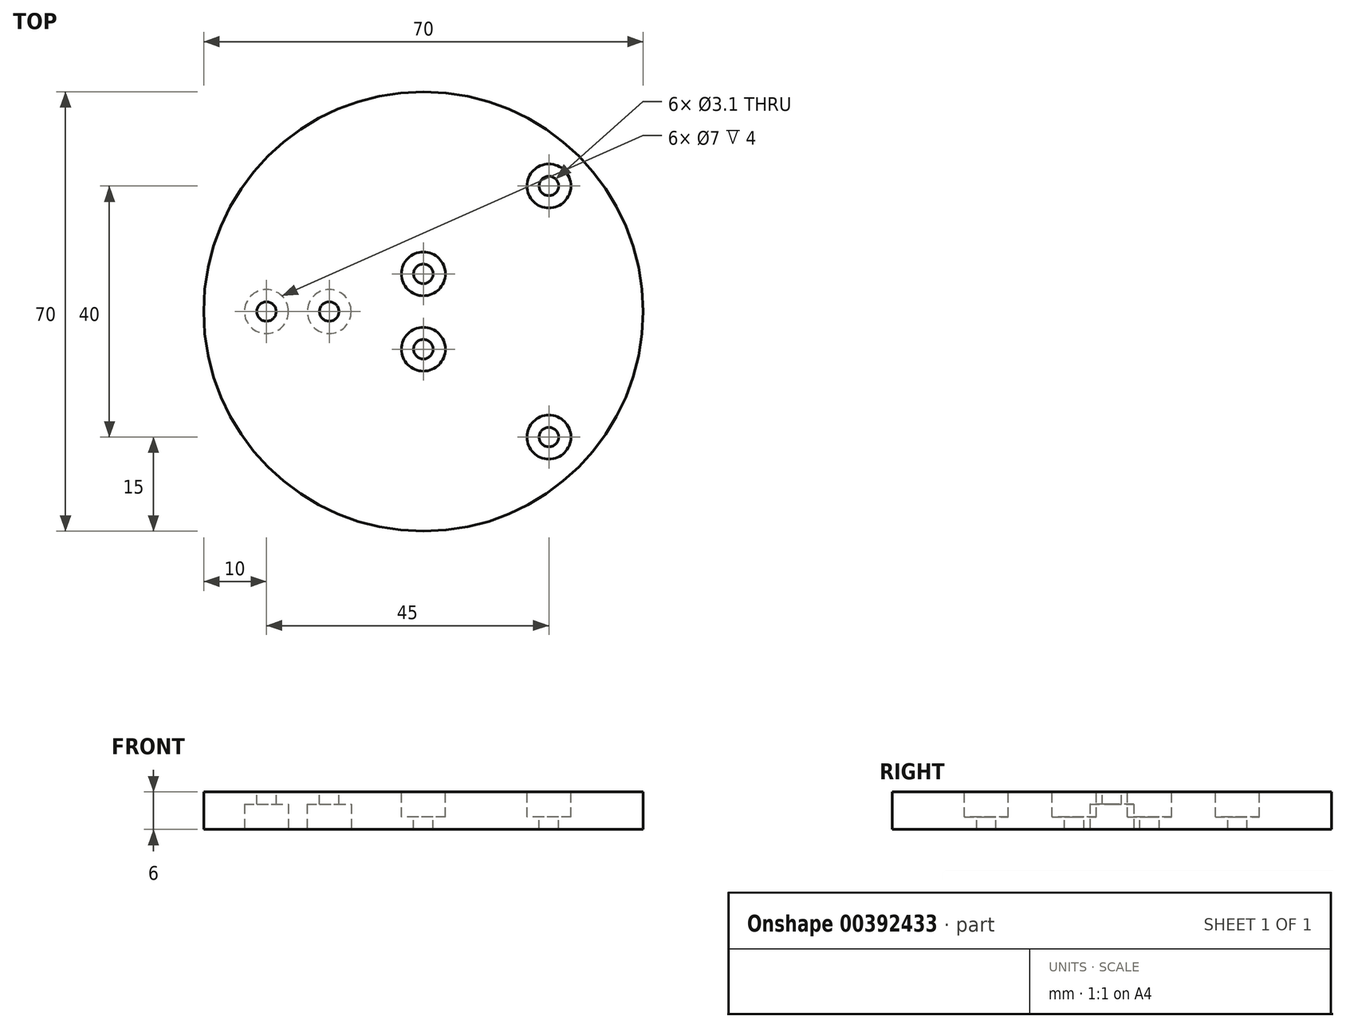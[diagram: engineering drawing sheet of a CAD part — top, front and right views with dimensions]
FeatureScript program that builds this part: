
annotation { "Feature Type Name" : "Feature", "Feature Type Description" : "" }
export const myFeature = defineFeature(function(context is Context, id is Id, definition is map)
    precondition{}
    {
        {
            var Q0;
            Q0=qCreatedBy(makeId("Top.planeOp"),FACE);
            var sketch = newSketch(context, id + "F0", { "sketchPlane" : qUnion([Q0])});
            skCircle(sketch, "E0", {"center": v(0, 0) * mm, "radius": 35 * mm});
            skSolve(sketch);
        }
        {
            var Q0;
            Q0=makeQuery(id+"F0.imprint","IMPRINT",FACE,{"disambiguationData":[TD([[makeQuery(id+"F0.imprint","IMPRINT",EDGE,{"derivedFrom":sQuery(id+"F0.wireOp",EDGE,"E0")}),1.0]])]});
            extrude(context, id + "F1", {"entities" : qUnion([Q0]), "depth" : 6 * mm});
        }
        {
            var Q0;
            Q0=makeQuery(id+"F1.opExtrude","CAP_FACE",FACE,{"disambiguationData":[OSD([sQuery(id+"F0.wireOp",EDGE,"E0")])],"isStart":false});
            var sketch = newSketch(context, id + "F2", { "sketchPlane" : qUnion([Q0])});
            skCircle(sketch, "E1", {"center": v(0, 6) * mm, "radius": 1.55 * mm});
            skCircle(sketch, "E2", {"center": v(0, -6) * mm, "radius": 1.55 * mm});
            skCircle(sketch, "E3", {"center": v(-15, 0) * mm, "radius": 1.55 * mm});
            skCircle(sketch, "E4", {"center": v(-25, 0) * mm, "radius": 1.55 * mm});
            skCircle(sketch, "E5", {"center": v(20, -20) * mm, "radius": 1.55 * mm});
            skCircle(sketch, "E6", {"center": v(20, 20) * mm, "radius": 1.55 * mm});
            skSolve(sketch);
        }
        {
            var Q0;
            Q0=makeQuery(id+"F2.imprint","IMPRINT",FACE,{"disambiguationData":[TD([[makeQuery(id+"F2.imprint","IMPRINT",EDGE,{"derivedFrom":sQuery(id+"F2.wireOp",EDGE,"E1")}),1.0]])]});
            var Q1;
            Q1=makeQuery(id+"F2.imprint","IMPRINT",FACE,{"disambiguationData":[TD([[makeQuery(id+"F2.imprint","IMPRINT",EDGE,{"derivedFrom":sQuery(id+"F2.wireOp",EDGE,"E2")}),1.0]])]});
            var Q2;
            Q2=makeQuery(id+"F2.imprint","IMPRINT",FACE,{"disambiguationData":[TD([[makeQuery(id+"F2.imprint","IMPRINT",EDGE,{"derivedFrom":sQuery(id+"F2.wireOp",EDGE,"E6")}),1.0]])]});
            var Q3;
            Q3=makeQuery(id+"F2.imprint","IMPRINT",FACE,{"disambiguationData":[TD([[makeQuery(id+"F2.imprint","IMPRINT",EDGE,{"derivedFrom":sQuery(id+"F2.wireOp",EDGE,"E5")}),1.0]])]});
            var Q4;
            Q4=makeQuery(id+"F2.imprint","IMPRINT",FACE,{"disambiguationData":[TD([[makeQuery(id+"F2.imprint","IMPRINT",EDGE,{"derivedFrom":sQuery(id+"F2.wireOp",EDGE,"E3")}),1.0]])]});
            var Q5;
            Q5=makeQuery(id+"F2.imprint","IMPRINT",FACE,{"disambiguationData":[TD([[makeQuery(id+"F2.imprint","IMPRINT",EDGE,{"derivedFrom":sQuery(id+"F2.wireOp",EDGE,"E4")}),1.0]])]});
            var Q6;
            Q6=makeQuery(id+"F2.imprint","IMPRINT",FACE,{"disambiguationData":[TD([[makeQuery(id+"F2.imprint","IMPRINT",EDGE,{"derivedFrom":sQuery(id+"F2.wireOp",EDGE,"hfZRwmrS-vUBX-50BD-5Ecu-MXVkSbwIy5IX")}),1.0]])]});
            var Q7;
            Q7=makeQuery(id+"F2.imprint","IMPRINT",FACE,{"disambiguationData":[TD([[makeQuery(id+"F2.imprint","IMPRINT",EDGE,{"derivedFrom":sQuery(id+"F2.wireOp",EDGE,"fXSNGoxq-e6GF-EdTq-bPJF-QqQfHw6qqzR7")}),1.0]])]});
            extrude(context, id + "F3", {"entities" : qUnion([Q0, Q1, Q2, Q3, Q4, Q5, Q6, Q7]), "operationType" : NewBodyOperationType.REMOVE, "endBound" : BoundingType.UP_TO_NEXT, "oppositeDirection" : true, "depth" : 25 * mm});
        }
        {
            var Q0;
            Q0=makeQuery(id+"F1.opExtrude","CAP_FACE",FACE,{"disambiguationData":[OSD([sQuery(id+"F0.wireOp",EDGE,"E0")])],"isStart":false});
            var sketch = newSketch(context, id + "F4", { "sketchPlane" : qUnion([Q0])});
            skCircle(sketch, "E7", {"center": v(0, -6) * mm, "radius": 3.5 * mm});
            skCircle(sketch, "E8", {"center": v(0, 6) * mm, "radius": 3.5 * mm});
            skCircle(sketch, "E9", {"center": v(20, -20) * mm, "radius": 3.5 * mm});
            skCircle(sketch, "E10", {"center": v(20, 20) * mm, "radius": 3.5 * mm});
            skSolve(sketch);
        }
        {
            var Q0;
            Q0=qSketchRegion(id+"F4",true);
            var Q1;
            Q1=makeQuery(id+"F4.imprint","IMPRINT",FACE,{"disambiguationData":[TD([[makeQuery(id+"F4.imprint","IMPRINT",EDGE,{"derivedFrom":makeQuery(id+"F3.boolean.opBoolean","COPY",EDGE,{"derivedFrom":makeQuery(id+"F3.opExtrude","CAP_EDGE",EDGE,{"disambiguationData":[OSD([sQuery(id+"F2.wireOp",EDGE,"E6")])],"isStart":true})})}),1.0]])]});
            var Q2;
            Q2=makeQuery(id+"F4.imprint","IMPRINT",FACE,{"disambiguationData":[TD([[makeQuery(id+"F4.imprint","IMPRINT",EDGE,{"derivedFrom":makeQuery(id+"F3.boolean.opBoolean","COPY",EDGE,{"derivedFrom":makeQuery(id+"F3.opExtrude","CAP_EDGE",EDGE,{"disambiguationData":[OSD([sQuery(id+"F2.wireOp",EDGE,"E5")])],"isStart":true})})}),1.0]])]});
            extrude(context, id + "F5", {"entities" : qUnion([Q0, Q1, Q2]), "operationType" : NewBodyOperationType.REMOVE, "oppositeDirection" : true, "depth" : 4 * mm});
        }
        {
            var Q0;
            Q0=makeQuery(id+"F1.opExtrude","CAP_FACE",FACE,{"disambiguationData":[OSD([sQuery(id+"F0.wireOp",EDGE,"E0")])],"isStart":true});
            var sketch = newSketch(context, id + "F6", { "sketchPlane" : qUnion([Q0])});
            skCircle(sketch, "E11", {"center": v(-25, 0) * mm, "radius": 3.5 * mm});
            skCircle(sketch, "E12", {"center": v(-15, 0) * mm, "radius": 3.5 * mm});
            skSolve(sketch);
        }
        {
            var Q0;
            Q0=qSketchRegion(id+"F6",true);
            extrude(context, id + "F7", {"entities" : qUnion([Q0]), "operationType" : NewBodyOperationType.REMOVE, "oppositeDirection" : true, "depth" : 4 * mm});
        }
    });
